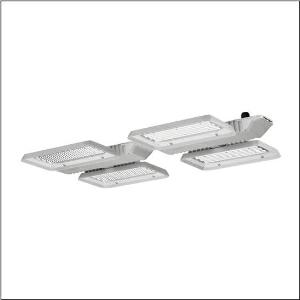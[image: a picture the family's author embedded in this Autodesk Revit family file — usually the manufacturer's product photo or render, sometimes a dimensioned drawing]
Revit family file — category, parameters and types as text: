
# Revit family: highbay_11_51hla1d24nca
name_source: partatom
category: Lighting Fixtures
units: mm (PartAtom-declared; Revit-internal decimal feet)

## family parameters
Cut with Voids When Loaded = No
Host = Face
Light Source = No
Part Type = Normal
Room Calculation Point = No
Round Connector Dimension = Use Diameter
Shared = No

## types (1)
- --- (1 x LED, 32370 lm, 189.6 W, 4000K)
    Apparent Load = 190 VA
    CIE Flux Codes = 88 95 99 100 99
    Color Rendering = 80
    Color Temperature = 4000K
    Default Elevation = 1800 mm
    Description = Highbay 11, LED high bay luminaire, primary light control with lens, of PMMA, light emission: direct distribution, primary light characteristic: symmetric, installation type: suspended mounting, surface-mounted, for 2x 2x LED, rated luminous flux: 32.370lm, luminous efficacy: 171lm/W, light colour: 840, colour temperature: 4000K, control gear: ECG DALI, with terminal, 5-pole, max. 2.5mm², mains connection: 230..240V, AC, 50/60Hz, rated input power: 190W, LED unit, of diecast aluminium, unplated, bead blasted, silver, length: 940mm, width: 500mm, height: 65mm, housing, of diecast aluminium, uncoated, bead blasted, silver, protection rating (complete): IP65, insulation class (complete): insulation class I (protective earthing), certification: CE, ENEC, VDE, UKCA, protection symbol: D, impact resistance: IK08 with glass or PC cover, permissible operating ambient temperature: -35..+45°C, reducing of maximum allowable ambient temperature of 5°C with ceiling mounting, corresponds to IFS (International Featured Standards) requirements for safety and quality in the food industry, packaging unit: 1 piece
    Height = 95 mm
    Lamp = 1 x LED
    Lamp Light Flux = 32370 lm
    Lamp Power = 189.6 W
    Lamp count = 1
    Length = 939 mm
    Luminous efficacy = 171 lm/W
    Manufacturer = Siteco
    ModVariant = No
    Model = 51HLA1D24NCA
    Mounting Place = Ceiling
    Mounting Type = Pendant
    Number of Poles = 1
    OnlyDefault = Yes
    Power Factor = 1
    Product Name = Highbay 11
    Product group = LED high bay luminaire
    ProductGroupID = 903
    Protection Class = Protection class I
    Protection Degree = IP 65
    RLX_Detail_Level = 1
    RLX_Emergency_Light_Flux = 0 lm
    RLX_Emergency_Type = 0
    RLX_Emergency_Type_DB = No
    RlxData = <blob elided: 100421 chars, md5=08ef3616>
    Socket = socket
    Standby Power = 0 W
    System Light Flux = 32370 lm
    System Power = 190 W
    Type Comments = factory setting: luminous flux: 100 % | dim-lin: 254 | 535 mA
    Type Image = l_1003428.jpg
    URL = http://relux.com
    VarID = @adj_146155
    Voltage = 0 V
    Weight = 0.00 kg
    Width = 501 mm

## geometry (parser evidence)
native form markers: Blend x4, Sweep x12
no freeform markers — native parametric forms only
